# Revit family: BE_50116.2_de_DE
name_source: partatom
category: Leuchten
revit_build: Autodesk Revit 2015 (Build: 20160512_0715(x64)
units: mm (PartAtom-declared; Revit-internal decimal feet)

## types (1)
- BEGA_50116.2_K3
    AC/DC = AC
    Aktualisierung = 2017-05-16T04:07:40
    BEGA_Dummy = Nein
    BEGA_IES = Ja
    BEGA_Intern = Ja
    BEGA_Intern_Konstruktion = Ja
    BEGA_Intern_an = Ja
    BEGA_Intern_aus = Ja
    Beschreibung = Wandeinbauleuchte
    Beschreibung_Sonderanfertigung = Hier können Sie Informationen zur Sonderanfertigung eintragen.
    Bestellnummer = 50116.2
    CE_Konformität = ja
    Datei für fotometrisches Netz = LI_50116.IES
    Einbau_in_Wärmedämmung = ungeeignet
    Einbautiefe = 65 mm
    Einbauöffnung = 68 mm
    Energieeffizienzklasse = LED A++ - A
    Farbfilter = 16777215
    Farbtemperatur = 3000 K
    Farbtemperaturverschiebung bei Dämpfen der Lampe = <Keine Auswahl>
    Farbwiedergabeindex = Ra > 80
    Frequenz = 50-60 Hz
    Hersteller = BEGA
    LED_Modulbezeichnung = LED-0676/830
    Lampe = LED 1.9 W
    Lampenlichtstrom = 335 lm
    Lastklassifizierung = Beleuchtung
    Lebensdauerkriterien = L70 = 50.000 h
    Leuchtenlichtstrom = 83 lm
    Logo = BEGA_Logo.png
    M_A = Nein
    M_G = Nein
    M_W = Nein
    Material_02 = BEGA_Oberfläche_Silber_matt
    Material_03 = BEGA_Oberfläche_Weiss_matt
    Material_05 = BEGA_Oberfläche_Aluminium Guss
    Material_06 = BEGA_Oberfläche_Edelstahl_gebürstet
    Material_09 = BEGA_Glas_klar
    Material_11 = BEGA_Glas_opal
    Material_15 = BEGA_Leuchtmedium_matt
    Material_17 = BEGA_Reflektor
    Modell = 50116.2
    Neigungswinkel = 0.00°
    Produktdatenblatt = http://www.bega.de
    Scheinlast = 0 VA
    Schutzklasse = I
    Sonderanfertigung = Nein
    Spannung = 240 V
    URL = http://www.bega.de
    Vorgabe-Ansicht = 0 mm  [stored 0 ft]

note: [stored X ft] marks values corroborated as IEEE doubles in the binary element streams (Revit-internal decimal feet)
